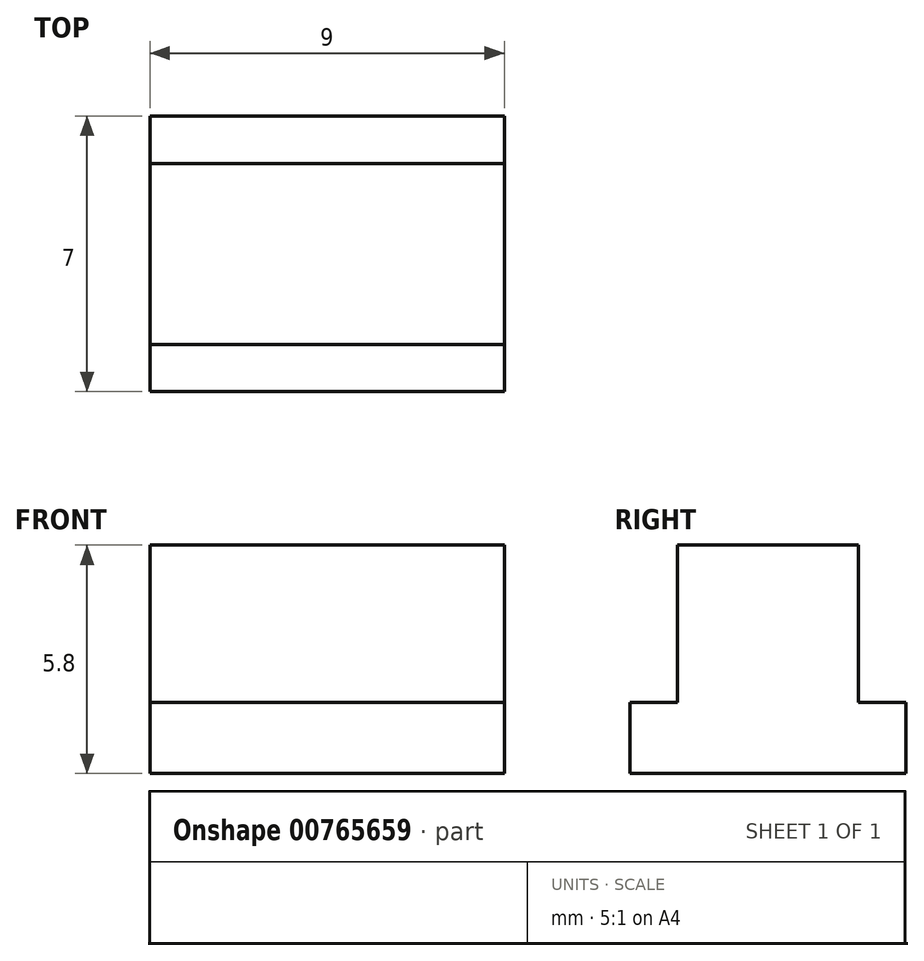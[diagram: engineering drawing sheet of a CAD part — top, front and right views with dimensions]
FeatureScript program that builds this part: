
annotation { "Feature Type Name" : "Feature", "Feature Type Description" : "" }
export const myFeature = defineFeature(function(context is Context, id is Id, definition is map)
    precondition{}
    {
        {
            var Q0;
            Q0=qCreatedBy(makeId("Top.planeOp"),FACE);
            var sketch = newSketch(context, id + "F0", { "sketchPlane" : qUnion([Q0])});
            skLineSegment(sketch, "E0.bottom", {"start": v(4.5, 3.5) * mm, "end": v(-4.5, 3.5) * mm});
            skLineSegment(sketch, "E0.top", {"start": v(4.5, -3.5) * mm, "end": v(-4.5, -3.5) * mm});
            skLineSegment(sketch, "E0.left", {"start": v(4.5, 3.5) * mm, "end": v(4.5, -3.5) * mm});
            skLineSegment(sketch, "E0.right", {"start": v(-4.5, 3.5) * mm, "end": v(-4.5, -3.5) * mm});
            skPoint(sketch, "E0.middle", {"position": v(0, 0) * mm});
            skSolve(sketch);
        }
        {
            var Q0;
            Q0=makeQuery(id+"F0.imprint","IMPRINT",FACE,{"disambiguationData":[TD([[makeQuery(id+"F0.imprint","IMPRINT",EDGE,{"derivedFrom":sQuery(id+"F0.wireOp",EDGE,"E0.bottom")}),1.0]])]});
            extrude(context, id + "F1", {"entities" : qUnion([Q0]), "depth" : 1.8 * mm, "offsetDistance" : 25 * mm});
        }
        {
            var Q0;
            Q0=makeQuery(id+"F1.opExtrude","CAP_FACE",FACE,{"disambiguationData":[OSD([sQuery(id+"F0.wireOp",EDGE,"E0.bottom"),sQuery(id+"F0.wireOp",EDGE,"E0.top"),sQuery(id+"F0.wireOp",EDGE,"E0.left"),sQuery(id+"F0.wireOp",EDGE,"E0.right")])],"isStart":false});
            var sketch = newSketch(context, id + "F2", { "sketchPlane" : qUnion([Q0])});
            skLineSegment(sketch, "E1.bottom", {"start": v(4.5, 2.3) * mm, "end": v(-4.5, 2.3) * mm});
            skLineSegment(sketch, "E1.top", {"start": v(4.5, -2.3) * mm, "end": v(-4.5, -2.3) * mm});
            skLineSegment(sketch, "E1.left", {"start": v(4.5, 2.3) * mm, "end": v(4.5, -2.3) * mm});
            skLineSegment(sketch, "E1.right", {"start": v(-4.5, 2.3) * mm, "end": v(-4.5, -2.3) * mm});
            skPoint(sketch, "E1.middle", {"position": v(0, 0) * mm});
            skSolve(sketch);
        }
        {
            var Q0;
            Q0 = qSketchRegion(id + "F2", true);
            extrude(context, id + "F3", {"entities" : qUnion([Q0]), "operationType" : NewBodyOperationType.ADD, "depth" : 4 * mm, "offsetDistance" : 25 * mm});
        }
    });
